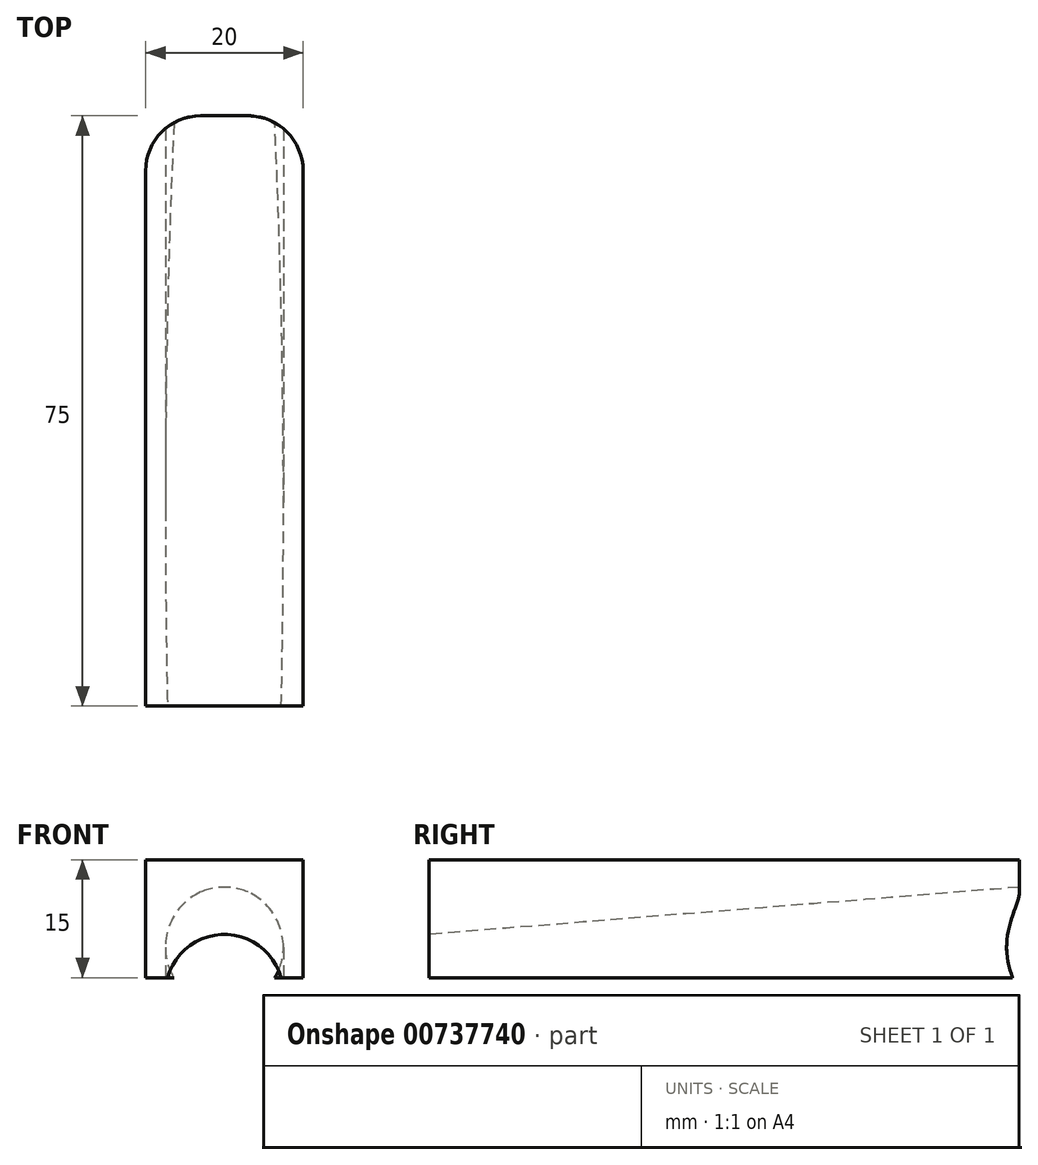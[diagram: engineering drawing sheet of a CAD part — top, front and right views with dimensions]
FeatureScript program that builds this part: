
annotation { "Feature Type Name" : "Feature", "Feature Type Description" : "" }
export const myFeature = defineFeature(function(context is Context, id is Id, definition is map)
    precondition{}
    {
        {
            var Q0;
            Q0=qCreatedBy(makeId("Top.planeOp"),FACE);
            var sketch = newSketch(context, id + "F0", { "sketchPlane" : qUnion([Q0])});
            skLineSegment(sketch, "E0.bottom", {"start": v(-10, -10) * mm, "end": v(10, -10) * mm});
            skLineSegment(sketch, "E0.top", {"start": v(-3, 65) * mm, "end": v(3, 65) * mm});
            skLineSegment(sketch, "E0.left", {"start": v(-10, -10) * mm, "end": v(-10, 58) * mm});
            skLineSegment(sketch, "E0.right", {"start": v(10, -10) * mm, "end": v(10, 58) * mm});
            skPoint(sketch, "E1.visualSharp", {"position": v(-10, 65) * mm});
            skArc(sketch, "E1.filletArc", {"start": v(-3, 65) * mm, "mid": v(-7.95, 62.95) * mm, "end": v(-10, 58) * mm});
            skPoint(sketch, "E2.visualSharp", {"position": v(10, 65) * mm});
            skArc(sketch, "E2.filletArc", {"start": v(10, 58) * mm, "mid": v(7.95, 62.95) * mm, "end": v(3, 65) * mm});
            skSolve(sketch);
        }
        {
            var Q0;
            Q0=makeQuery(id+"F0.imprint","IMPRINT",FACE,{"disambiguationData":[TD([[makeQuery(id+"F0.imprint","IMPRINT",EDGE,{"derivedFrom":sQuery(id+"F0.wireOp",EDGE,"E0.bottom")}),1.0]])]});
            extrude(context, id + "F1", {"entities" : qUnion([Q0]), "depth" : 15 * mm, "offsetDistance" : 25 * mm});
        }
        {
            var Q0;
            Q0=makeQuery(id+"F1.opExtrude","SWEPT_FACE",FACE,{"disambiguationData":[OSD([sQuery(id+"F0.wireOp",EDGE,"E0.top")])]});
            var sketch = newSketch(context, id + "F2", { "sketchPlane" : qUnion([Q0])});
            skCircle(sketch, "E3", {"center": v(0, 4) * mm, "radius": 7.5 * mm});
            skSolve(sketch);
        }
        {
            var Q0;
            Q0=qCreatedBy(makeId("Right.planeOp"),FACE);
            var sketch = newSketch(context, id + "F3", { "sketchPlane" : qUnion([Q0])});
            skLineSegment(sketch, "E4", {"start": v(65, 5) * mm, "end": v(-10, -1) * mm});
            skSolve(sketch);
        }
        {
            var Q0;
            Q0 = qSketchRegion(id + "F2", true);
            var Q1;
            Q1 = qConstructionFilter(qBodyType(qCreatedBy(id + "F3" ,EDGE), BodyType.WIRE), ConstructionObject.NO);
            sweep(context, id + "F4", {"operationType" : NewBodyOperationType.REMOVE, "profiles" : qUnion([Q0]), "path" : qUnion([Q1])});
        }
        {
            var Q0;
            Q0=qCreatedBy(makeId("Right.planeOp"),FACE);
            cPlane(context, id + "F5", {"entities" : qUnion([Q0]), "cplaneType" : CPlaneType.OFFSET, "offset" : 25 * mm, "width" : 150 * mm, "height" : 150 * mm});
        }
    });
